# Revit family: MAD-464_Sirena analógica
name_source: partatom
category: Dispositivos de alarma de incendios
revit_build: Autodesk Revit 2017 (Build: 20190508_0315(x64)
units: mm (PartAtom-declared; Revit-internal decimal feet)

## family parameters
Anfitrión = Cara
Compartido = No
Corte con vacíos al cargar = No
Cota de conector redondo = Diámetro de uso
Mantener orientación de anotación = No
Punto de cálculo de habitación = No
Tipo de pieza = Normal

## types (1)
- MAD-464-I
    Altura = 100 mm
    Anchura = 100 mm
    Carga eléctrica = Otro
    Certificación = EN 54-3 y EN 54-17
    Comentarios de tipo = Las sirenas analógicas, gama MAD-46X-I, son el medio de transmisión de alarma para el personal que ocupa un edificio y así iniciar la evacuación en caso necesario. Son un elemento básico en cualquier instalación junto con los pulsadores y detectores.
    Conexionado = 2 x 1.5 mm² trenzado y apantallado
    Consumo en alarma = < 20 mA
    Consumo en reposo = < 300 μA
    Cuerpo = ABS Rojo
    Código de montaje = PDETMAD-464-I
    Descripción = Sirena analógica con aislador incorporado para conexión directa al lazo. Marca Detnov, modelo MAD-464-I. Bajo consumo. 32 tonos  y 3 volúmenes configurables (Bajo, Medio, Alto). Potencia acústica de 78.3 dBA a 104.6 dBA dependiendo del tono seleccionado. Ocupa una dirección en el lazo. Color rojo. Uso de interior. IP33C. Base alta para entrada de tubo visto. Dimensiones: 100 x 75 mm.
    Elevación por defecto = 1219 mm
    Fabricante = Detnov Security
    Fases = 1
    Humedad relativa = 95% sin condensación
    Imagen de tipo = <Ninguno>
    Modelo = Sirena analógica MAD-464-I
    Número máximo de sirenas en el lazo = 20 sirenas a 1 km / 10 sirenas a 2 km
    Potencia total = 0 VA
    Profundidad = 75 mm
    Teléfono = (+34) 93 371 60 25
    Temperatura trabajo = De -10ºC a 60ºC
    Tensión de trabajo = De 22 a 38VDC
    URL = https://www.detnov.com
    Voltaje = 230 V
    Volumen = De 78,3 dB(A) a 104,6 dB(A) dependiendo del tono
    Índice IP = IP33C
